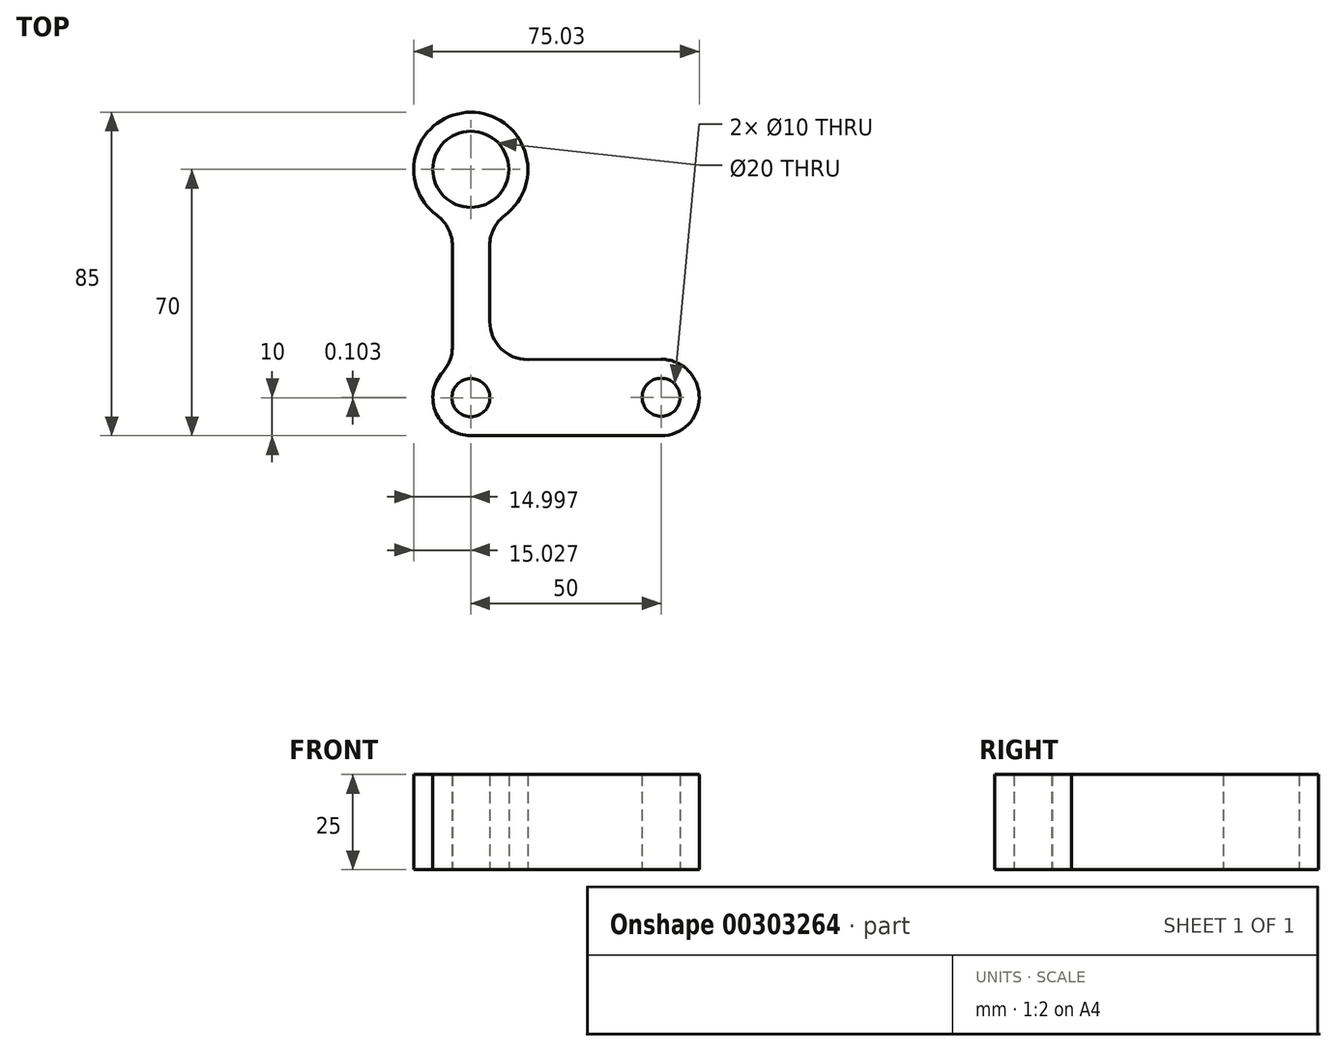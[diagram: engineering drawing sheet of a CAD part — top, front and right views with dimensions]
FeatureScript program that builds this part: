
annotation { "Feature Type Name" : "Feature", "Feature Type Description" : "" }
export const myFeature = defineFeature(function(context is Context, id is Id, definition is map)
    precondition{}
    {
        {
            var Q0;
            Q0=qCreatedBy(makeId("Top.planeOp"),FACE);
            var sketch = newSketch(context, id + "F0", { "sketchPlane" : qUnion([Q0])});
            skLineSegment(sketch, "E0", {"start": v(-40.85, -49.96) * mm, "end": v(9.15, -49.96) * mm});
            skLineSegment(sketch, "E1", {"start": v(19.15, -39.96) * mm, "end": v(19.15, -39.86) * mm});
            skPoint(sketch, "E2.visualSharp", {"position": v(19.15, -29.96) * mm});
            skArc(sketch, "E2.filletArc", {"start": v(19.15, -39.86) * mm, "mid": v(16.21, -32.78) * mm, "end": v(9.13, -29.86) * mm});
            skPoint(sketch, "E3.visualSharp", {"position": v(19.15, -49.96) * mm});
            skArc(sketch, "E3.filletArc", {"start": v(9.15, -49.96) * mm, "mid": v(16.22, -47.03) * mm, "end": v(19.15, -39.96) * mm});
            skPoint(sketch, "E4.visualSharp", {"position": v(-50.85, -49.96) * mm});
            skArc(sketch, "E4.filletArc", {"start": v(-50.85, -39.96) * mm, "mid": v(-47.92, -47.03) * mm, "end": v(-40.85, -49.96) * mm});
            skPoint(sketch, "E5.end.orphan", {"position": v(-50.85, 20.04) * mm});
            skPoint(sketch, "E6.visualSharp", {"position": v(-31, -39.42) * mm});
            skCircle(sketch, "E7", {"center": v(9.15, -39.86) * mm, "radius": 5 * mm});
            skCircle(sketch, "E8", {"center": v(-40.85, -39.96) * mm, "radius": 5 * mm});
            skPoint(sketch, "E9.end.orphan", {"position": v(-30.85, -29.96) * mm});
            skCircle(sketch, "E10", {"center": v(-40.88, 20.04) * mm, "radius": 10 * mm});
            skPoint(sketch, "E11.endSnap0", {"position": v(-37.95, -39.42) * mm});
            skArc(sketch, "E12", {"start": v(-31.88, 8.04) * mm, "mid": v(-40.94, 35.04) * mm, "end": v(-49.78, 7.97) * mm});
            skPoint(sketch, "E13.trimOffspring.end.orphan", {"position": v(-45.72, -39.42) * mm});
            skPoint(sketch, "E11.end.orphan", {"position": v(-35.45, -29.96) * mm});
            skLineSegment(sketch, "E14", {"start": v(-31.42, -39.42) * mm, "end": v(-31, -39.42) * mm});
            skLineSegment(sketch, "E15", {"start": v(-35.88, -19.96) * mm, "end": v(-35.88, 0.04) * mm});
            skLineSegment(sketch, "E16", {"start": v(-45.72, -26.58) * mm, "end": v(-45.72, -0.08) * mm});
            skLineSegment(sketch, "E17", {"start": v(-25.85, -29.96) * mm, "end": v(9.13, -29.86) * mm});
            skPoint(sketch, "E18.visualSharp", {"position": v(-35.88, -29.99) * mm});
            skArc(sketch, "E18.filletArc", {"start": v(-35.88, -19.96) * mm, "mid": v(-32.94, -27.04) * mm, "end": v(-25.85, -29.96) * mm});
            skPoint(sketch, "E19.visualSharp", {"position": v(-35.88, 5.9) * mm});
            skArc(sketch, "E19.filletArc", {"start": v(-31.88, 8.04) * mm, "mid": v(-34.83, 4.51) * mm, "end": v(-35.88, 0.04) * mm});
            skPoint(sketch, "E20.visualSharp", {"position": v(-45.72, 5.84) * mm});
            skArc(sketch, "E20.filletArc", {"start": v(-45.72, -0.08) * mm, "mid": v(-46.8, 4.43) * mm, "end": v(-49.78, 7.97) * mm});
            skLineSegment(sketch, "E21", {"start": v(-48.38, -39.42) * mm, "end": v(-48.38, -39.42) * mm});
            skPoint(sketch, "E22.visualSharp", {"position": v(-50.85, -29.96) * mm});
            skLineSegment(sketch, "E23", {"start": v(-50.85, -39.96) * mm, "end": v(-50.85, -39.96) * mm});
            skArc(sketch, "E24.filletArc", {"start": v(-48.29, -33.27) * mm, "mid": v(-50.19, -36.38) * mm, "end": v(-50.85, -39.96) * mm});
            skLineSegment(sketch, "E25.trimOffspring", {"start": v(-35.88, -39.42) * mm, "end": v(-35.88, -39.42) * mm});
            skLineSegment(sketch, "E26.trimOffspring", {"start": v(-45.82, -39.42) * mm, "end": v(-45.72, -39.42) * mm});
            skLineSegment(sketch, "E27.trimOffspring", {"start": v(-25.91, -29.96) * mm, "end": v(-25.85, -29.96) * mm});
            skPoint(sketch, "E28.visualSharp", {"position": v(-45.72, -31.22) * mm});
            skArc(sketch, "E29.filletArc", {"start": v(-48.29, -33.27) * mm, "mid": v(-46.38, -30.16) * mm, "end": v(-45.72, -26.58) * mm});
            skSolve(sketch);
        }
        {
            var Q0;
            Q0 = qSketchRegion(id + "F0", true);
            extrude(context, id + "F1", {"entities" : qUnion([Q0]), "depth" : 25 * mm});
        }
    });
